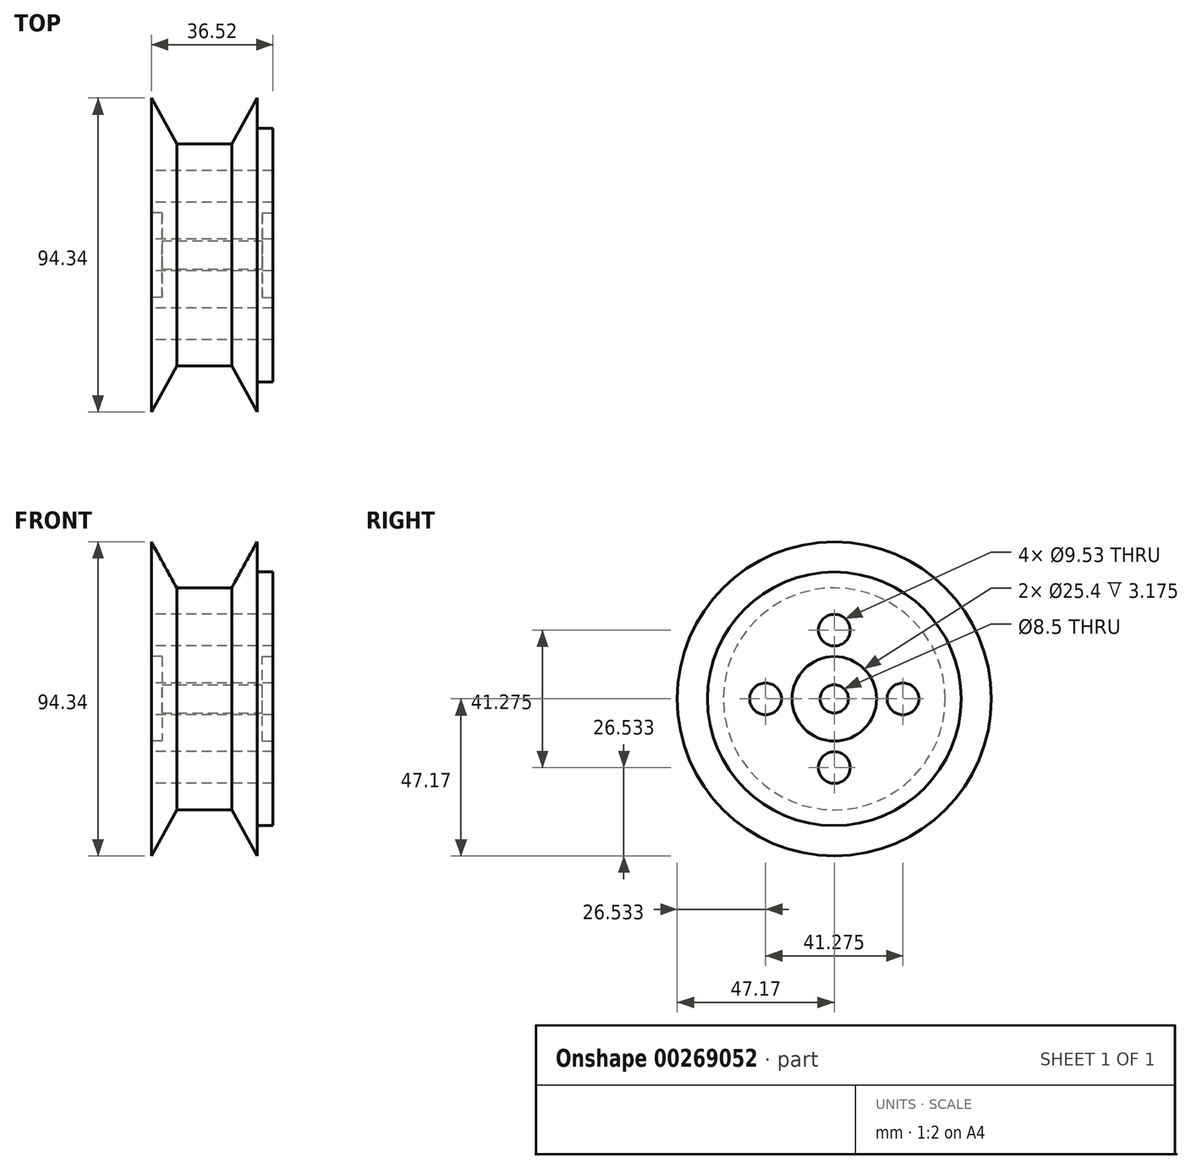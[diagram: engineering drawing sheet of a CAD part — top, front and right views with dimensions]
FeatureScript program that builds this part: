
annotation { "Feature Type Name" : "Feature", "Feature Type Description" : "" }
export const myFeature = defineFeature(function(context is Context, id is Id, definition is map)
    precondition{}
    {
        {
            var Q0;
            Q0=qCreatedBy(makeId("Front.planeOp"),FACE);
            var sketch = newSketch(context, id + "F0", { "sketchPlane" : qUnion([Q0])});
            skLineSegment(sketch, "E0.bottom", {"start": v(-15.87, 41.6) * mm, "end": v(15.87, 41.6) * mm});
            skLineSegment(sketch, "E0.top", {"start": v(-15.87, -41.6) * mm, "end": v(15.87, -41.6) * mm});
            skLineSegment(sketch, "E0.left", {"start": v(-15.87, 41.6) * mm, "end": v(-15.88, -41.6) * mm});
            skLineSegment(sketch, "E0.right", {"start": v(15.88, 41.6) * mm, "end": v(15.87, -41.6) * mm});
            skLineSegment(sketch, "E1", {"start": v(8.26, 33.34) * mm, "end": v(-8.26, 33.34) * mm});
            skLineSegment(sketch, "E2.MirrorCS", {"start": v(8.26, -33.34) * mm, "end": v(-8.26, -33.34) * mm});
            skLineSegment(sketch, "E3", {"start": v(-8.26, 33.34) * mm, "end": v(-12.8, 41.6) * mm});
            skLineSegment(sketch, "E4", {"start": v(8.26, 33.34) * mm, "end": v(12.8, 41.6) * mm});
            skLineSegment(sketch, "E5.MirrorCS", {"start": v(8.26, -33.34) * mm, "end": v(12.8, -41.6) * mm});
            skLineSegment(sketch, "E6.MirrorCS", {"start": v(-8.26, -33.34) * mm, "end": v(-12.8, -41.6) * mm});
            skLineSegment(sketch, "E7.bottom", {"start": v(15.87, -38.1) * mm, "end": v(20.64, -38.1) * mm});
            skLineSegment(sketch, "E7.top", {"start": v(15.87, 38.1) * mm, "end": v(20.64, 38.1) * mm});
            skLineSegment(sketch, "E7.left", {"start": v(15.88, -38.1) * mm, "end": v(15.88, 38.1) * mm});
            skLineSegment(sketch, "E7.right", {"start": v(20.64, -38.1) * mm, "end": v(20.64, 38.1) * mm});
            skLineSegment(sketch, "E8", {"start": v(-15.88, 0) * mm, "end": v(20.64, 0) * mm});
            skCircle(sketch, "E9", {"center": v(0, 0) * mm, "radius": 4.76 * mm});
            skLineSegment(sketch, "E10", {"start": v(-15.87, 41.6) * mm, "end": v(-15.87, 47.17) * mm});
            skLineSegment(sketch, "E11", {"start": v(-15.88, 47.17) * mm, "end": v(-12.8, 41.6) * mm});
            skLineSegment(sketch, "E12.MirrorCS", {"start": v(15.88, 47.17) * mm, "end": v(12.8, 41.6) * mm});
            skLineSegment(sketch, "E13.MirrorCS", {"start": v(15.87, 41.6) * mm, "end": v(15.87, 47.17) * mm});
            skLineSegment(sketch, "E14.MirrorCS", {"start": v(-15.88, -47.17) * mm, "end": v(-12.8, -41.6) * mm});
            skLineSegment(sketch, "E15.MirrorCS", {"start": v(-15.87, -41.6) * mm, "end": v(-15.87, -47.17) * mm});
            skLineSegment(sketch, "E16.MirrorCS", {"start": v(15.88, -47.17) * mm, "end": v(12.8, -41.6) * mm});
            skLineSegment(sketch, "E17.MirrorCS", {"start": v(15.87, -41.6) * mm, "end": v(15.87, -47.17) * mm});
            skSolve(sketch);
        }
        {
            var Q0;
            Q0=makeQuery(id+"F0.imprint","IMPRINT",FACE,{"disambiguationData":[TD([[makeQuery(id+"F0.imprint","IMPRINT",EDGE,{"derivedFrom":sQuery(id+"F0.wireOp",EDGE,"E1")}),1.0]])]});
            var Q1;
            {var subQ0=sQuery(id+"F0.wireOp",EDGE,"E7.top");Q1=makeQuery(id+"F0.imprint","IMPRINT",FACE,{"disambiguationData":[TD([[makeQuery(id+"F0.imprint","IMPRINT",EDGE,{"derivedFrom":subQ0}),-1.0]])]});}
            var Q2;
            {var subQ0=sQuery(id+"F0.wireOp",EDGE,"E9");var subQ1=sQuery(id+"F0.wireOp",EDGE,"E8");var subQ2=makeQuery(id+"F0.imprint","INTERSECT",VERTEX,{"disambiguationData":[OD(0.0)],"derivedFrom":[subQ1,subQ0]});Q2=makeQuery(id+"F0.imprint","IMPRINT",FACE,{"disambiguationData":[TD([[makeQuery(id+"F0.imprint","IMPRINT",EDGE,{"disambiguationData":[TD([[subQ2,-1.0]])],"derivedFrom":subQ1}),1.0]])]});}
            var Q3;
            {var subQ0=sQuery(id+"F0.wireOp",EDGE,"E10");Q3=makeQuery(id+"F0.imprint","IMPRINT",FACE,{"disambiguationData":[TD([[makeQuery(id+"F0.imprint","IMPRINT",EDGE,{"derivedFrom":subQ0}),-1.0]])]});}
            var Q4;
            {var subQ2=sQuery(id+"F0.wireOp",EDGE,"E12.MirrorCS");Q4=makeQuery(id+"F0.imprint","IMPRINT",FACE,{"disambiguationData":[TD([[makeQuery(id+"F0.imprint","IMPRINT",EDGE,{"derivedFrom":subQ2}),1.0]])]});}
            var Q5;
            Q5=sQuery(id+"F0.wireOp",EDGE,"E8");
            revolve(context, id + "F1", {"entities" : qUnion([Q0, Q1, Q2, Q3, Q4]), "axis" : qUnion([Q5]), "revolveType" : RevolveType.FULL});
        }
        {
            var Q0;
            Q0=makeQuery(id+"F1.opRevolve","SWEPT_FACE",FACE,{"disambiguationData":[OSD([sQuery(id+"F0.wireOp",EDGE,"E7.right")])]});
            var sketch = newSketch(context, id + "F2", { "sketchPlane" : qUnion([Q0])});
            skCircle(sketch, "E18", {"center": v(0, 0) * mm, "radius": 4.25 * mm});
            skCircle(sketch, "E19", {"center": v(0, 0) * mm, "radius": 12.7 * mm});
            skSolve(sketch);
        }
        {
            var Q0;
            Q0=makeQuery(id+"F2.imprint","IMPRINT",FACE,{"disambiguationData":[TD([[makeQuery(id+"F2.imprint","IMPRINT",EDGE,{"derivedFrom":sQuery(id+"F2.wireOp",EDGE,"E18")}),1.0]])]});
            extrude(context, id + "F3", {"entities" : qUnion([Q0]), "operationType" : NewBodyOperationType.REMOVE, "endBound" : BoundingType.THROUGH_ALL, "oppositeDirection" : true, "depth" : 25.4 * mm});
        }
        {
            var Q0;
            Q0=makeQuery(id+"F2.imprint","IMPRINT",FACE,{"disambiguationData":[TD([[makeQuery(id+"F2.imprint","IMPRINT",EDGE,{"derivedFrom":sQuery(id+"F2.wireOp",EDGE,"E18")}),-1.0]])]});
            extrude(context, id + "F4", {"entities" : qUnion([Q0]), "operationType" : NewBodyOperationType.REMOVE, "oppositeDirection" : true, "depth" : 3.17 * mm});
        }
        {
            var Q0;
            Q0=makeQuery(id+"F1.opRevolve","SWEPT_FACE",FACE,{"disambiguationData":[OSD([sQuery(id+"F0.wireOp",EDGE,"E0.left")])]});
            var sketch = newSketch(context, id + "F5", { "sketchPlane" : qUnion([Q0])});
            skCircle(sketch, "E20", {"center": v(0, 0) * mm, "radius": 4.25 * mm});
            skCircle(sketch, "E21", {"center": v(0, 0) * mm, "radius": 12.7 * mm});
            skCircle(sketch, "E22", {"center": v(0, 20.64) * mm, "radius": 4.76 * mm});
            skCircle(sketch, "E23", {"center": v(-20.64, 0) * mm, "radius": 4.76 * mm});
            skCircle(sketch, "E24", {"center": v(20.64, 0) * mm, "radius": 4.76 * mm});
            skCircle(sketch, "E25", {"center": v(0, -20.64) * mm, "radius": 4.76 * mm});
            skSolve(sketch);
        }
        {
            var Q0;
            Q0=makeQuery(id+"F5.imprint","IMPRINT",FACE,{"disambiguationData":[TD([[makeQuery(id+"F5.imprint","IMPRINT",EDGE,{"derivedFrom":sQuery(id+"F5.wireOp",EDGE,"E20")}),1.0]])]});
            extrude(context, id + "F6", {"entities" : qUnion([Q0]), "operationType" : NewBodyOperationType.REMOVE, "oppositeDirection" : true, "depth" : 3.17 * mm});
        }
        {
            var Q0;
            Q0=makeQuery(id+"F5.imprint","IMPRINT",FACE,{"disambiguationData":[TD([[makeQuery(id+"F5.imprint","IMPRINT",EDGE,{"derivedFrom":sQuery(id+"F5.wireOp",EDGE,"E22")}),1.0]])]});
            var Q1;
            Q1=makeQuery(id+"F5.imprint","IMPRINT",FACE,{"disambiguationData":[TD([[makeQuery(id+"F5.imprint","IMPRINT",EDGE,{"derivedFrom":sQuery(id+"F5.wireOp",EDGE,"E24")}),1.0]])]});
            var Q2;
            Q2=makeQuery(id+"F5.imprint","IMPRINT",FACE,{"disambiguationData":[TD([[makeQuery(id+"F5.imprint","IMPRINT",EDGE,{"derivedFrom":sQuery(id+"F5.wireOp",EDGE,"E25")}),1.0]])]});
            var Q3;
            Q3=makeQuery(id+"F5.imprint","IMPRINT",FACE,{"disambiguationData":[TD([[makeQuery(id+"F5.imprint","IMPRINT",EDGE,{"derivedFrom":sQuery(id+"F5.wireOp",EDGE,"E23")}),1.0]])]});
            extrude(context, id + "F7", {"entities" : qUnion([Q0, Q1, Q2, Q3]), "operationType" : NewBodyOperationType.REMOVE, "endBound" : BoundingType.THROUGH_ALL, "oppositeDirection" : true, "depth" : 25.4 * mm});
        }
    });
